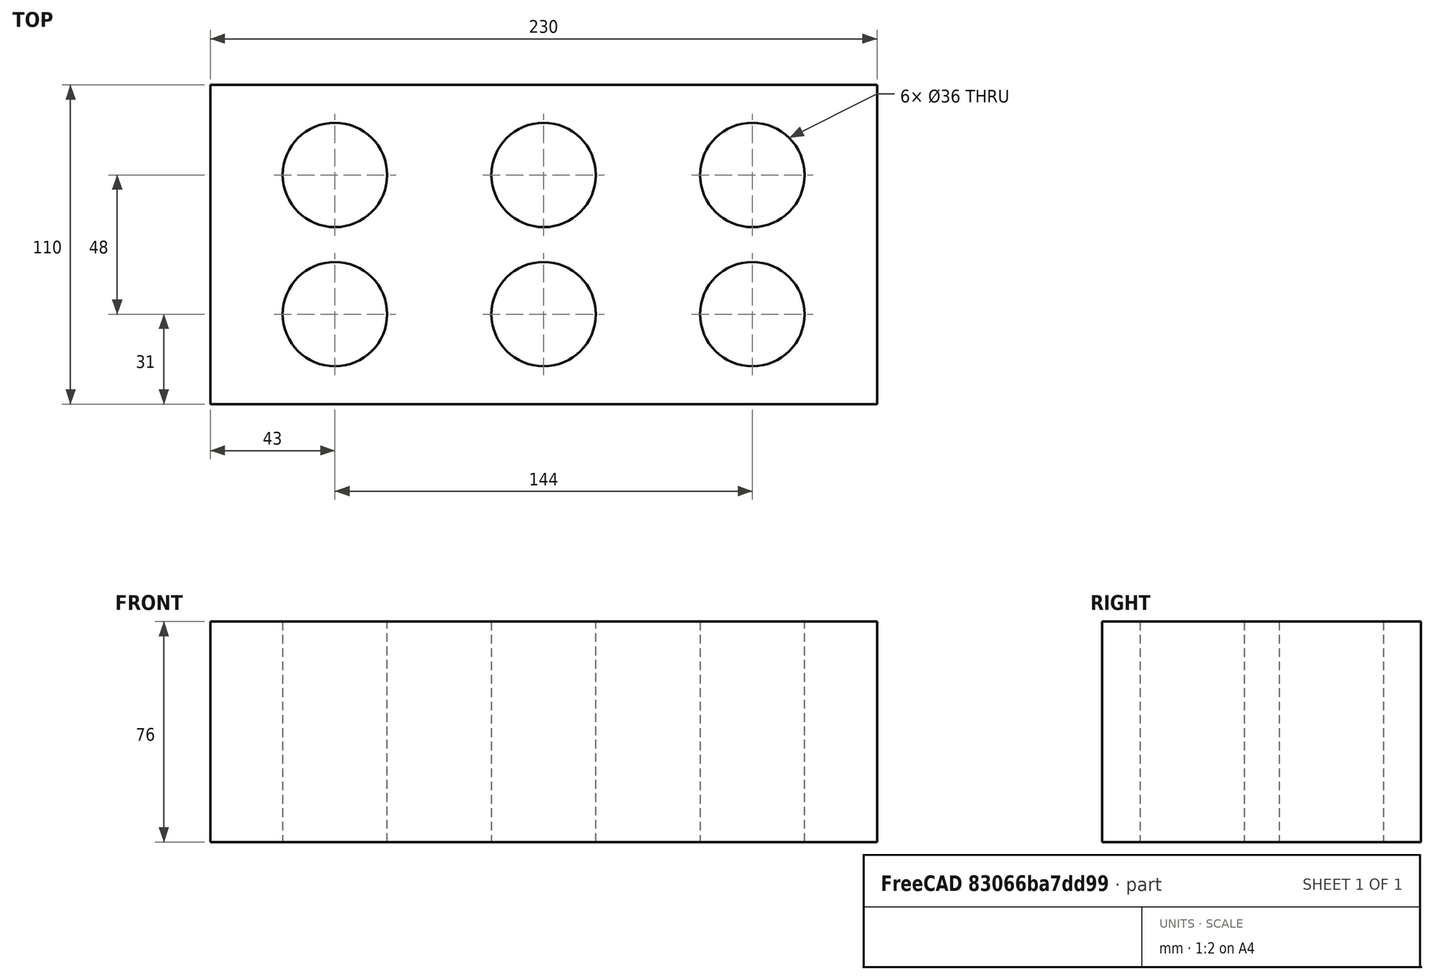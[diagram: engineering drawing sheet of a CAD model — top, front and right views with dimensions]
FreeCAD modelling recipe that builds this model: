
FCSTD DOCUMENT  (FreeCAD 0.21R33771 (Git))
Label: OJT1_T09R02_totxo
License: All rights reserved
LicenseURL: http://en.wikipedia.org/wiki/All_rights_reserved
objects: Part::Cylinder×6, Part::Box×1, Part::MultiFuse×1, Part::Cut×1
note: 9 computed .brp shape members not serialized (recipe doc carries the construction recipe); baked Part::Feature solids carry a one-line shape summary decoded from their .brp

FEATURE [Part::Box] Box  label="Cube"
  AttacherType = Attacher::AttachEngine3D
  Height = 76
  Length = 230
  Width = 110
FEATURE [Part::Cylinder] Cylinder  label="forat"
  Angle = 360
  AttacherType = Attacher::AttachEngine3D
  FirstAngle = 0
  Height = 80
  Placement = pos=(43,31,-2) rot=(0,0,1;0rad)
  Radius = 18
  SecondAngle = 0
FEATURE [Part::Cylinder] Cylinder001  label="forat001"
  Angle = 360
  AttacherType = Attacher::AttachEngine3D
  FirstAngle = 0
  Height = 80
  Placement = pos=(43,79,-2) rot=(0,0,1;0rad)
  Radius = 18
  SecondAngle = 0
FEATURE [Part::Cylinder] Cylinder002  label="forat002"
  Angle = 360
  AttacherType = Attacher::AttachEngine3D
  FirstAngle = 0
  Height = 80
  Placement = pos=(115,31,-2) rot=(0,0,1;0rad)
  Radius = 18
  SecondAngle = 0
FEATURE [Part::Cylinder] Cylinder003  label="forat003"
  Angle = 360
  AttacherType = Attacher::AttachEngine3D
  FirstAngle = 0
  Height = 80
  Placement = pos=(187,31,-2) rot=(0,0,1;0rad)
  Radius = 18
  SecondAngle = 0
FEATURE [Part::Cylinder] Cylinder004  label="forat004"
  Angle = 360
  AttacherType = Attacher::AttachEngine3D
  FirstAngle = 0
  Height = 80
  Placement = pos=(115,79,-2) rot=(0,0,1;0rad)
  Radius = 18
  SecondAngle = 0
FEATURE [Part::Cylinder] Cylinder005  label="forat005"
  Angle = 360
  AttacherType = Attacher::AttachEngine3D
  FirstAngle = 0
  Height = 80
  Placement = pos=(187,79,-2) rot=(0,0,1;0rad)
  Radius = 18
  SecondAngle = 0
FEATURE [Part::MultiFuse] Fusion  label="forats"
  Refine = true
  Shapes = -> [Cylinder,Cylinder001,Cylinder002,Cylinder003,Cylinder004,Cylinder005]
FEATURE [Part::Cut] Cut  label="totxo"
  Base = -> Box
  Refine = true
  Tool = -> Fusion
